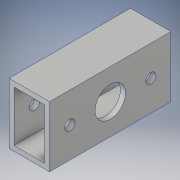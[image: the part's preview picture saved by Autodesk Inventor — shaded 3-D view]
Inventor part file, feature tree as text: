
AUTODESK INVENTOR PART (.ipt)
format: ipt  version: 2017 (Build 210142000, 142)  size: 143,872 bytes
history: native  units: in
note: dims shown in document units (in); Inventor stores cm internally (conversion verified against a paired STEP export)
features: sketch x3, extrude x2, hole x2, split x2, pattern_linear x1
ambient origin geometry x8: Origin, YZ Plane, XZ Plane, XY Plane, X Axis, Y Axis, Z Axis, Center Point
bodies: Solid1 (feature_tree)
feature tree (10):
  extrude  "Extrusion1"  Depth=1.5in
  extrude  "Extrusion2"  Depth=0.125in TaperAngle=0.0deg
  pattern_linear  "Rectangular Pattern1"  Spacing1=5.0in  [1 undecoded]
  hole  "Hole1"  [1 undecoded]
  hole  "Hole2"  [1 undecoded]
  sketch  "Sketch3"  dims[d5=0.25in d6=5.0in d7=0.0in d8=1.5748in d10=1.0in d11=1.0in d12=1.0in d13=0.625in d14=0.75in d15=0.375in d16=0.25in d17=0.5635in d18=1.0in d19=0.8108in d20=1.0in d21=1.0in d22=0.75in d23=0.75in d24=0.375in d25=0.25in d26=0.5635in d27=1.0in d28=0.8108in d29=1.0in d30=1.0in]
  split  "Split1"
  split  "Split2"
  sketch  "Sketch1"  dims[d0=1.0in d1=1.5in]
  sketch  "Sketch2"  dims[d2=0.125in d3=5.0in d4=0.0in]
note: 3 required parameter values undecoded (feature->parameter linkage not recoverable at this tier; creation-order binding heuristic only, values carry confidence <= 0.55)
